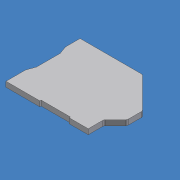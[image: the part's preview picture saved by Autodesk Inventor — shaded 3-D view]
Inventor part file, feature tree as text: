
AUTODESK INVENTOR PART (.ipt)
format: ipt  version: 2012 (Build 160160000, 160)  size: 80,384 bytes
history: native  units: mm (DEFAULTED — no unit token found)
features: extrude x1, sketch x1
ambient origin geometry x8: Origin, YZ Plane, XZ Plane, XY Plane, X Axis, Y Axis, Z Axis, Center Point
bodies: Solid1 (feature_tree)
feature tree (2):
  extrude  "Extrusion1"  [1 undecoded]
  sketch  "Skizze_1"  dims[d0=1.6mm d1=0.0mm]
note: 1 required parameter value undecoded (feature->parameter linkage not recoverable at this tier; creation-order binding heuristic only, values carry confidence <= 0.55)
